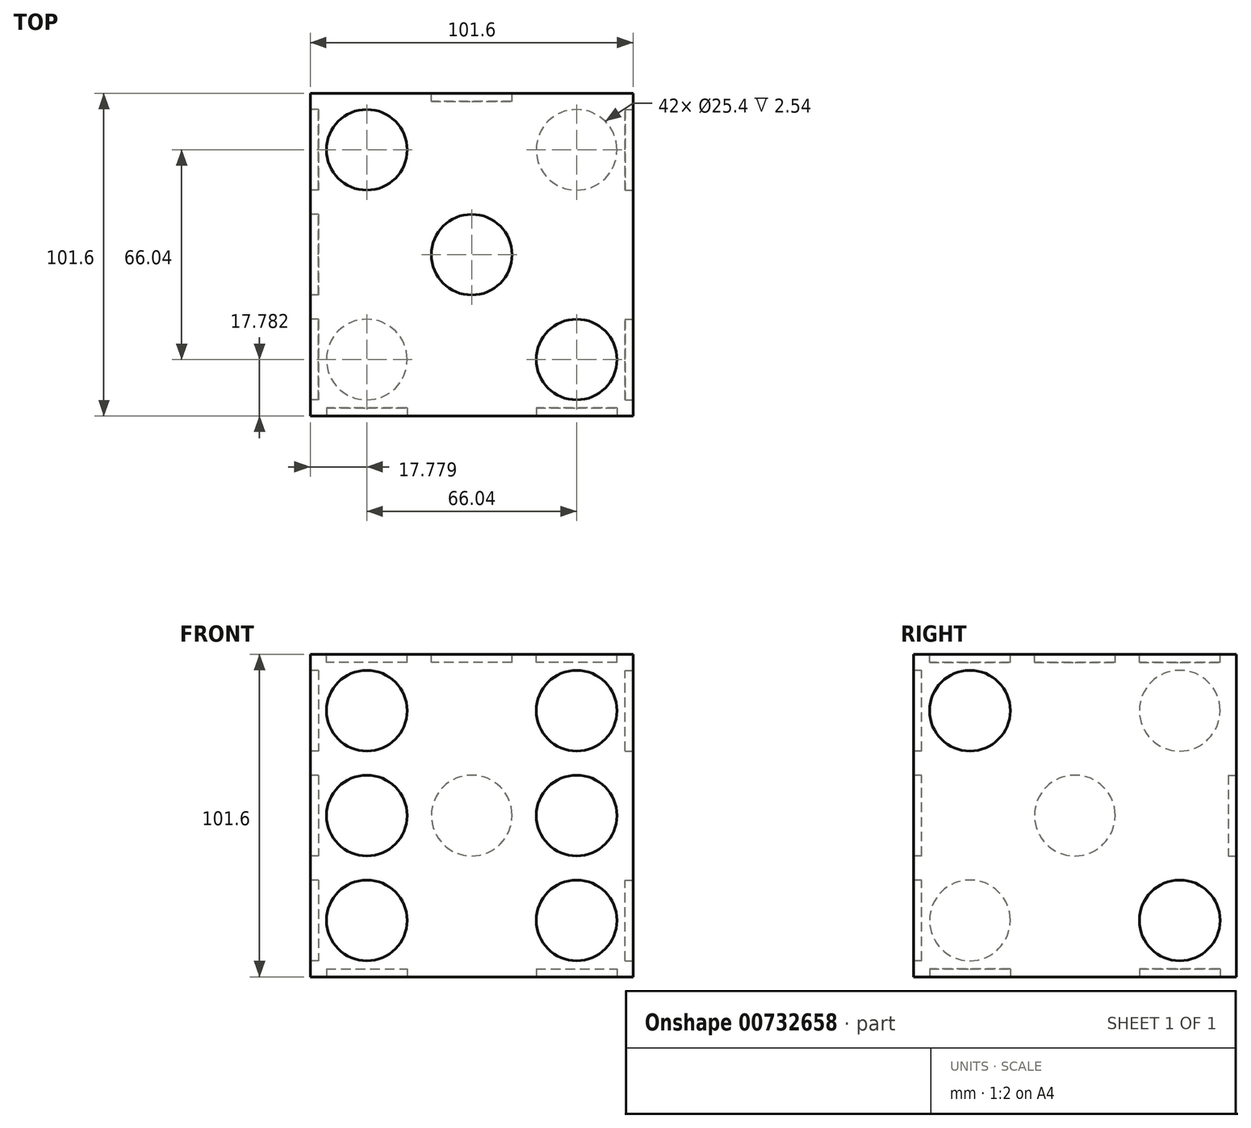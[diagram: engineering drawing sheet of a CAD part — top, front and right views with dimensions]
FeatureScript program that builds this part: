
annotation { "Feature Type Name" : "Feature", "Feature Type Description" : "" }
export const myFeature = defineFeature(function(context is Context, id is Id, definition is map)
    precondition{}
    {
        {
            var Q0;
            Q0=qCreatedBy(makeId("Top.planeOp"),FACE);
            var sketch = newSketch(context, id + "F0", { "sketchPlane" : qUnion([Q0])});
            skLineSegment(sketch, "E0.bottom", {"start": v(-55.5, 38.76) * mm, "end": v(46.1, 38.76) * mm});
            skLineSegment(sketch, "E0.top", {"start": v(-55.5, -62.84) * mm, "end": v(46.1, -62.84) * mm});
            skLineSegment(sketch, "E0.left", {"start": v(-55.5, 38.76) * mm, "end": v(-55.5, -62.84) * mm});
            skLineSegment(sketch, "E0.right", {"start": v(46.1, 38.76) * mm, "end": v(46.1, -62.84) * mm});
            skSolve(sketch);
        }
        {
            var Q0;
            Q0 = qSketchRegion(id + "F0", true);
            extrude(context, id + "F1", {"entities" : qUnion([Q0]), "depth" : 101.6 * mm, "offsetDistance" : 25.4 * mm});
        }
        {
            var Q0;
            Q0=makeQuery(id+"F1.opExtrude","SWEPT_FACE",FACE,{"disambiguationData":[OSD([sQuery(id+"F0.wireOp",EDGE,"E0.top")])]});
            var sketch = newSketch(context, id + "F2", { "sketchPlane" : qUnion([Q0])});
            skCircle(sketch, "E1", {"center": v(-37.71, 17.78) * mm, "radius": 12.7 * mm});
            skCircle(sketch, "E2.0.1.0", {"center": v(-37.71, 50.8) * mm, "radius": 12.7 * mm});
            skCircle(sketch, "E2.0.2.0", {"center": v(-37.71, 83.82) * mm, "radius": 12.7 * mm});
            skCircle(sketch, "E3", {"center": v(28.33, 17.78) * mm, "radius": 12.7 * mm});
            skCircle(sketch, "E4.0.1.0", {"center": v(28.33, 50.8) * mm, "radius": 12.7 * mm});
            skCircle(sketch, "E4.0.2.0", {"center": v(28.33, 83.82) * mm, "radius": 12.7 * mm});
            skLineSegment(sketch, "E4.direction1", {"start": v(28.33, 17.78) * mm, "end": v(53.73, 17.78) * mm, "construction": true});
            skLineSegment(sketch, "E4.direction2", {"start": v(28.33, 17.78) * mm, "end": v(28.33, 50.8) * mm, "construction": true});
            skSolve(sketch);
        }
        {
            var Q0;
            Q0 = qSketchRegion(id + "F2", true);
            extrude(context, id + "F3", {"entities" : qUnion([Q0]), "operationType" : NewBodyOperationType.REMOVE, "oppositeDirection" : true, "depth" : 2.54 * mm, "offsetDistance" : 25.4 * mm});
        }
        {
            var Q0;
            Q0=makeQuery(id+"F1.opExtrude","SWEPT_FACE",FACE,{"disambiguationData":[OSD([sQuery(id+"F0.wireOp",EDGE,"E0.bottom")])]});
            var sketch = newSketch(context, id + "F4", { "sketchPlane" : qUnion([Q0])});
            skCircle(sketch, "E5", {"center": v(4.7, 50.8) * mm, "radius": 12.7 * mm});
            skSolve(sketch);
        }
        {
            var Q0;
            Q0 = qSketchRegion(id + "F4", true);
            extrude(context, id + "F5", {"entities" : qUnion([Q0]), "operationType" : NewBodyOperationType.REMOVE, "oppositeDirection" : true, "depth" : 2.54 * mm, "offsetDistance" : 25.4 * mm});
        }
        {
            var Q0;
            Q0=makeQuery(id+"F1.opExtrude","SWEPT_FACE",FACE,{"disambiguationData":[OSD([sQuery(id+"F0.wireOp",EDGE,"E0.left")])]});
            var sketch = newSketch(context, id + "F6", { "sketchPlane" : qUnion([Q0])});
            skCircle(sketch, "E6", {"center": v(-20.98, 83.82) * mm, "radius": 12.7 * mm});
            skCircle(sketch, "E7", {"center": v(12.04, 50.8) * mm, "radius": 12.7 * mm});
            skCircle(sketch, "E8.0.1.0", {"center": v(-20.98, 17.78) * mm, "radius": 12.7 * mm});
            skCircle(sketch, "E8.1.0.0", {"center": v(45.06, 83.82) * mm, "radius": 12.7 * mm});
            skCircle(sketch, "E8.1.1.0", {"center": v(45.06, 17.78) * mm, "radius": 12.7 * mm});
            skLineSegment(sketch, "E8.direction1", {"start": v(-20.98, 83.82) * mm, "end": v(45.06, 83.82) * mm, "construction": true});
            skLineSegment(sketch, "E8.direction2", {"start": v(-20.98, 83.82) * mm, "end": v(-20.98, 17.78) * mm, "construction": true});
            skSolve(sketch);
        }
        {
            var Q0;
            Q0 = qSketchRegion(id + "F6", true);
            extrude(context, id + "F7", {"entities" : qUnion([Q0]), "operationType" : NewBodyOperationType.REMOVE, "oppositeDirection" : true, "depth" : 2.54 * mm, "offsetDistance" : 25.4 * mm});
        }
        {
            var Q0;
            Q0=makeQuery(id+"F1.opExtrude","SWEPT_FACE",FACE,{"disambiguationData":[OSD([sQuery(id+"F0.wireOp",EDGE,"E0.right")])]});
            var sketch = newSketch(context, id + "F8", { "sketchPlane" : qUnion([Q0])});
            skCircle(sketch, "E9", {"center": v(-45.06, 83.82) * mm, "radius": 12.7 * mm});
            skCircle(sketch, "E10", {"center": v(20.98, 17.78) * mm, "radius": 12.7 * mm});
            skSolve(sketch);
        }
        {
            var Q0;
            Q0 = qSketchRegion(id + "F8", true);
            extrude(context, id + "F9", {"entities" : qUnion([Q0]), "operationType" : NewBodyOperationType.REMOVE, "oppositeDirection" : true, "depth" : 2.54 * mm, "offsetDistance" : 25.4 * mm});
        }
        {
            var Q0;
            Q0=makeQuery(id+"F1.opExtrude","CAP_FACE",FACE,{"disambiguationData":[OSD([sQuery(id+"F0.wireOp",EDGE,"E0.bottom"),sQuery(id+"F0.wireOp",EDGE,"E0.top"),sQuery(id+"F0.wireOp",EDGE,"E0.left"),sQuery(id+"F0.wireOp",EDGE,"E0.right")])],"isStart":false});
            var sketch = newSketch(context, id + "F10", { "sketchPlane" : qUnion([Q0])});
            skCircle(sketch, "E11", {"center": v(-37.71, 20.98) * mm, "radius": 12.7 * mm});
            skCircle(sketch, "E12", {"center": v(-4.7, -12.04) * mm, "radius": 12.7 * mm});
            skCircle(sketch, "E13", {"center": v(28.33, -45.06) * mm, "radius": 12.7 * mm});
            skSolve(sketch);
        }
        {
            var Q0;
            Q0 = qSketchRegion(id + "F10", true);
            extrude(context, id + "F11", {"entities" : qUnion([Q0]), "operationType" : NewBodyOperationType.REMOVE, "oppositeDirection" : true, "depth" : 2.54 * mm, "offsetDistance" : 25.4 * mm});
        }
        {
            var Q0;
            Q0=makeQuery(id+"F1.opExtrude","CAP_FACE",FACE,{"disambiguationData":[OSD([sQuery(id+"F0.wireOp",EDGE,"E0.bottom"),sQuery(id+"F0.wireOp",EDGE,"E0.top"),sQuery(id+"F0.wireOp",EDGE,"E0.left"),sQuery(id+"F0.wireOp",EDGE,"E0.right")])],"isStart":true});
            var sketch = newSketch(context, id + "F12", { "sketchPlane" : qUnion([Q0])});
            skCircle(sketch, "E14", {"center": v(-37.71, 45.06) * mm, "radius": 12.7 * mm});
            skCircle(sketch, "E15.0.1.0", {"center": v(-37.71, -20.98) * mm, "radius": 12.7 * mm});
            skCircle(sketch, "E15.1.0.0", {"center": v(28.33, 45.06) * mm, "radius": 12.7 * mm});
            skCircle(sketch, "E15.1.1.0", {"center": v(28.33, -20.98) * mm, "radius": 12.7 * mm});
            skLineSegment(sketch, "E15.direction1", {"start": v(-37.71, 45.06) * mm, "end": v(28.33, 45.06) * mm, "construction": true});
            skLineSegment(sketch, "E15.direction2", {"start": v(-37.71, 45.06) * mm, "end": v(-37.71, -20.98) * mm, "construction": true});
            skSolve(sketch);
        }
        {
            var Q0;
            Q0 = qSketchRegion(id + "F12", true);
            extrude(context, id + "F13", {"entities" : qUnion([Q0]), "operationType" : NewBodyOperationType.REMOVE, "oppositeDirection" : true, "depth" : 2.54 * mm, "offsetDistance" : 25.4 * mm});
        }
    });
